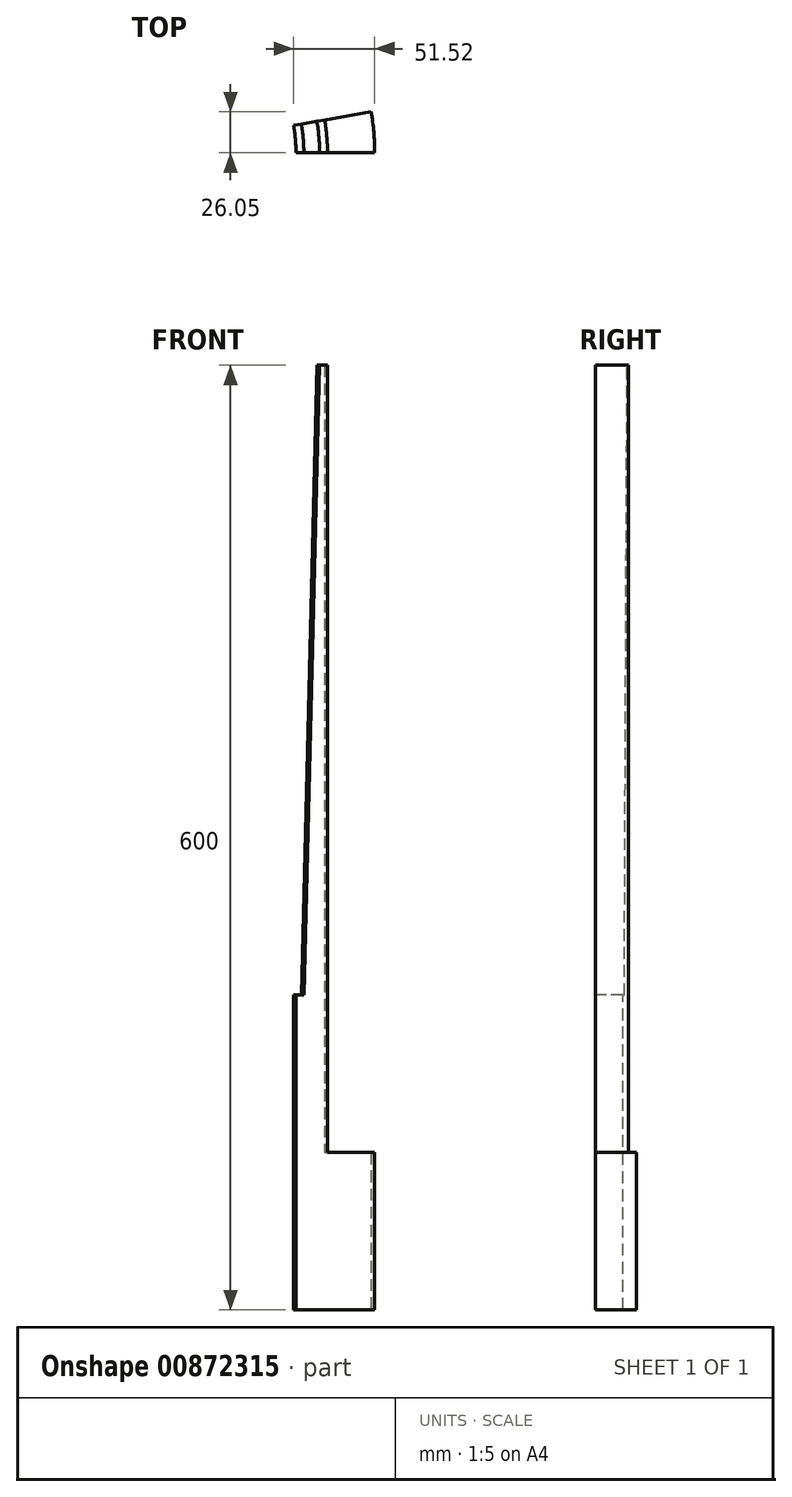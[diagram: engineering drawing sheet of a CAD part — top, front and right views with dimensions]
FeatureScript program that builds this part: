
annotation { "Feature Type Name" : "Feature", "Feature Type Description" : "" }
export const myFeature = defineFeature(function(context is Context, id is Id, definition is map)
    precondition{}
    {
        {
            var Q0;
            Q0=qCreatedBy(makeId("Front.planeOp"),FACE);
            var sketch = newSketch(context, id + "F0", { "sketchPlane" : qUnion([Q0])});
            skLineSegment(sketch, "E0", {"start": v(0, 0) * mm, "end": v(0, 810) * mm, "construction": true});
            skLineSegment(sketch, "E1", {"start": v(100, 0) * mm, "end": v(100, 200) * mm});
            skLineSegment(sketch, "E2", {"start": v(100, 200) * mm, "end": v(105, 200) * mm});
            skLineSegment(sketch, "E3", {"start": v(105, 200) * mm, "end": v(115, 600) * mm});
            skLineSegment(sketch, "E4", {"start": v(115, 600) * mm, "end": v(120, 600) * mm});
            skLineSegment(sketch, "E5", {"start": v(120, 600) * mm, "end": v(120, 100) * mm});
            skLineSegment(sketch, "E6", {"start": v(120, 100) * mm, "end": v(150, 100) * mm});
            skLineSegment(sketch, "E7", {"start": v(150, 100) * mm, "end": v(150, 0) * mm});
            skLineSegment(sketch, "E8", {"start": v(150, 0) * mm, "end": v(100, 0) * mm});
            skLineSegment(sketch, "E9", {"start": v(100, 210) * mm, "end": v(105.25, 210) * mm});
            skLineSegment(sketch, "E10", {"start": v(105.25, 210) * mm, "end": v(115.25, 610) * mm});
            skLineSegment(sketch, "E11", {"start": v(115.25, 610) * mm, "end": v(120, 610) * mm});
            skLineSegment(sketch, "E12", {"start": v(120, 610) * mm, "end": v(120, 710) * mm});
            skLineSegment(sketch, "E13", {"start": v(120, 710) * mm, "end": v(150, 710) * mm});
            skLineSegment(sketch, "E14", {"start": v(150, 710) * mm, "end": v(150, 810) * mm});
            skLineSegment(sketch, "E15", {"start": v(150, 810) * mm, "end": v(100, 810) * mm});
            skLineSegment(sketch, "E16", {"start": v(100, 810) * mm, "end": v(100, 210) * mm});
            skSolve(sketch);
        }
        {
            var Q0;
            Q0=makeQuery(id+"F0.imprint","IMPRINT",FACE,{"disambiguationData":[TD([[makeQuery(id+"F0.imprint","IMPRINT",EDGE,{"derivedFrom":sQuery(id+"F0.wireOp",EDGE,"E1")}),-1.0]])]});
            var Q1;
            Q1=sQuery(id+"F0.wireOp",EDGE,"E0");
            revolve(context, id + "F1", {"surfaceOperationType" : NewSurfaceOperationType.NEW, "entities" : qUnion([Q0]), "axis" : qUnion([Q1]), "revolveType" : RevolveType.ONE_DIRECTION, "angle" : 10 * degree});
        }
    });
